# Revit family: Sanitary_Accessories_Johnson-Suisse_Swift_Glass_Shelf_60cm_Tempered
name_source: partatom
category: Plumbing Fixtures
revit_build: Autodesk Revit 2015 (Build: 20140606_1530(x64)
units: mm (PartAtom-declared; Revit-internal decimal feet)

## types (1)
- Swift Glass Shelf 60cm Tempered
    BIMobject category = Accessories
    Brand url = http://www.johnsonsuisse.com.au
    Design country = Spain
    EAN code = https://9325304004648
    Edition number = 1
    IFC Classification = Furnishing Element
    Manufacturer country = China
    Manufacturer name = Johnson Suisse
    Material main = Metal
    Material secondary = Chrome
    NBS Reference Code = 35-77-06
    NBS Reference Description = Bathroom Shelves
    Nominal height = 35 mm  [stored 0.114829 ft]
    Nominal width = 600 mm  [stored 1.9685 ft]
    Product Guid = 630e678e-6bec-4fc7-a3fc-d72f9367d226
    Product SKU = GDC150145
    Product data url = https://bimobject.com
    Product family = Swift
    Product group = Accessories
    Product url = https://johnsonsuisse.com.au
    QR code = http://bimobject.com
    Technical description = https://johnsonsuisse.com.au
    Type = swift_glass_shelf_60cm_tempered : Default
    UNSPSC Code = 301815
    Uniclass 1.4 Code = L824
    Uniclass 1.4 Description = Bathroom, toilet furniture and fittings
    Uniclass 2.0 Code = PR-35-77-06
    Uniclass 2.0 Description = Bathroom Shelves
    Uniclass 2015 Code = Pr_40_30_78_06
    Uniclass 2015 Name = Bathroom shelves
    Weight Net (Kg) = 1.328

note: [stored X ft] marks values corroborated as IEEE doubles in the binary element streams (Revit-internal decimal feet)

## geometry (parser evidence)
native form markers: Sweep x5
no freeform markers — native parametric forms only
